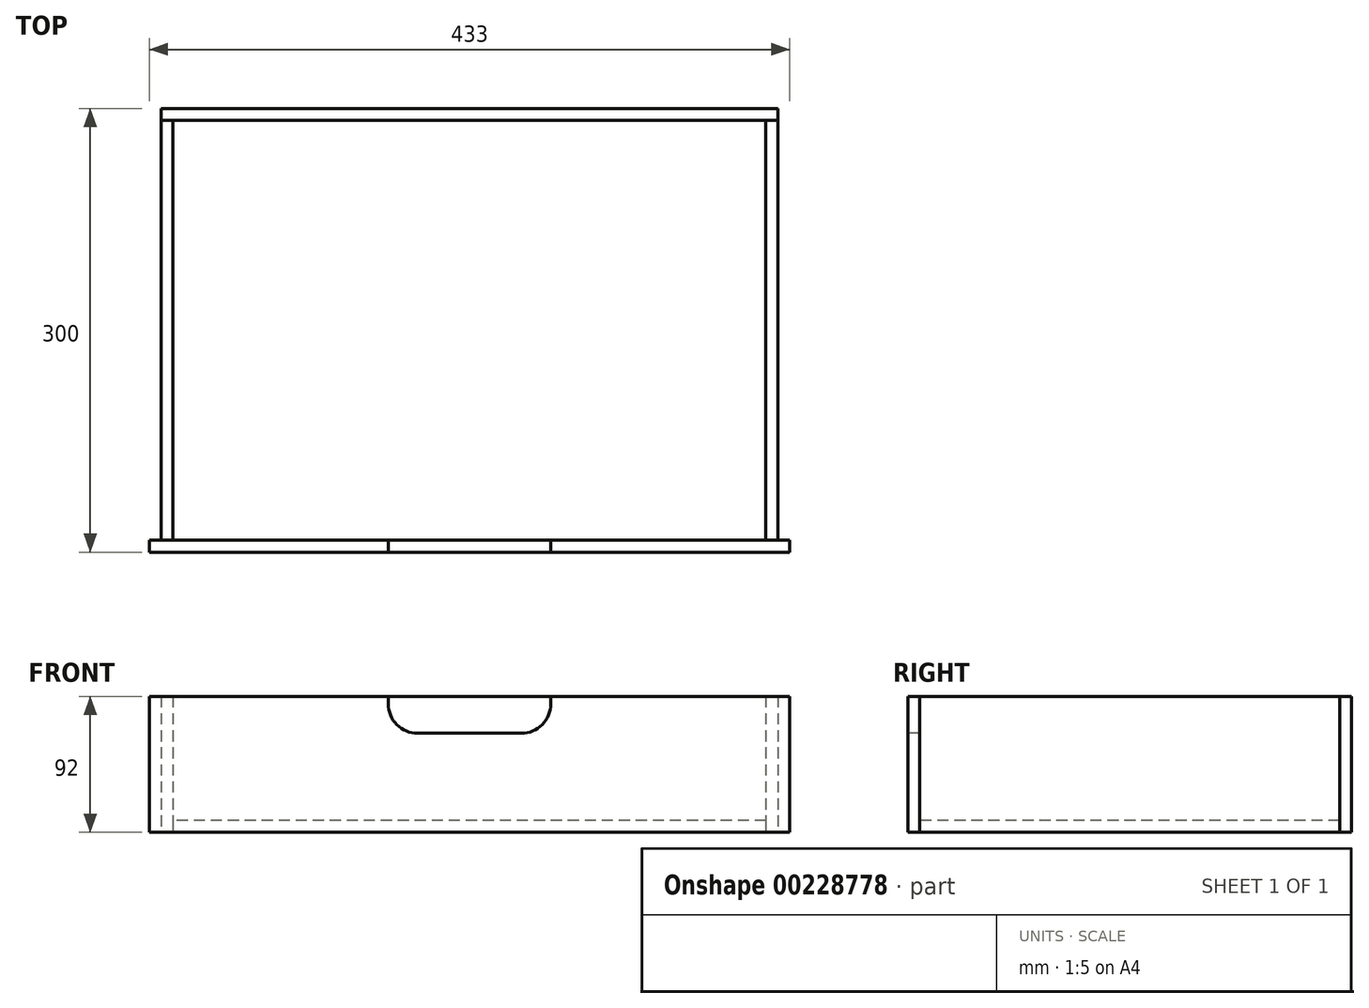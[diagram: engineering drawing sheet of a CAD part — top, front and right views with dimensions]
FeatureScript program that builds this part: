
annotation { "Feature Type Name" : "Feature", "Feature Type Description" : "" }
export const myFeature = defineFeature(function(context is Context, id is Id, definition is map)
    precondition{}
    {
        {
            var Q0;
            Q0=qCreatedBy(makeId("Front.planeOp"),FACE);
            var sketch = newSketch(context, id + "F0", { "sketchPlane" : qUnion([Q0])});
            skLineSegment(sketch, "E0.bottom", {"start": v(216.5, 46) * mm, "end": v(-216.5, 46) * mm});
            skLineSegment(sketch, "E0.top", {"start": v(216.5, -46) * mm, "end": v(-216.5, -46) * mm});
            skLineSegment(sketch, "E0.left", {"start": v(216.5, 46) * mm, "end": v(216.5, -46) * mm});
            skLineSegment(sketch, "E0.right", {"start": v(-216.5, 46) * mm, "end": v(-216.5, -46) * mm});
            skPoint(sketch, "E0.middle", {"position": v(0, 0) * mm});
            skSolve(sketch);
        }
        {
            var Q0;
            Q0=makeQuery(id+"F0.imprint","IMPRINT",FACE,{"disambiguationData":[TD([[makeQuery(id+"F0.imprint","IMPRINT",EDGE,{"derivedFrom":sQuery(id+"F0.wireOp",EDGE,"E0.bottom")}),1.0]])]});
            extrude(context, id + "F1", {"entities" : qUnion([Q0]), "depth" : 8 * mm});
        }
        {
            var Q0;
            Q0=makeQuery(id+"F1.opExtrude","CAP_FACE",FACE,{"disambiguationData":[OSD([sQuery(id+"F0.wireOp",EDGE,"E0.bottom"),sQuery(id+"F0.wireOp",EDGE,"E0.top"),sQuery(id+"F0.wireOp",EDGE,"E0.left"),sQuery(id+"F0.wireOp",EDGE,"E0.right")])],"isStart":false});
            var sketch = newSketch(context, id + "F2", { "sketchPlane" : qUnion([Q0])});
            skLineSegment(sketch, "E1.bottom", {"start": v(55, 21) * mm, "end": v(-55, 21) * mm});
            skLineSegment(sketch, "E1.top", {"start": v(55, 46) * mm, "end": v(-55, 46) * mm});
            skLineSegment(sketch, "E1.left", {"start": v(55, 21) * mm, "end": v(55, 46) * mm});
            skLineSegment(sketch, "E1.right", {"start": v(-55, 21) * mm, "end": v(-55, 46) * mm});
            skPoint(sketch, "E1.middle", {"position": v(0, 33.5) * mm});
            skSolve(sketch);
        }
        {
            var Q0;
            Q0=makeQuery(id+"F2.imprint","IMPRINT",FACE,{"disambiguationData":[TD([[makeQuery(id+"F2.imprint","IMPRINT",EDGE,{"derivedFrom":sQuery(id+"F2.wireOp",EDGE,"E1.bottom")}),-1.0]])]});
            extrude(context, id + "F3", {"entities" : qUnion([Q0]), "operationType" : NewBodyOperationType.REMOVE, "endBound" : BoundingType.UP_TO_NEXT, "oppositeDirection" : true, "depth" : 25 * mm});
        }
        {
            var Q0;
            Q0=makeQuery(id+"F3.boolean.opBoolean","COPY",EDGE,{"derivedFrom":makeQuery(id+"F3.opExtrude","SWEPT_EDGE",EDGE,{"disambiguationData":[OSD([sQuery(id+"F2.wireOp",EDGE,"E1.bottom"),sQuery(id+"F2.wireOp",EDGE,"E1.right")])]})});
            var Q1;
            Q1=makeQuery(id+"F3.boolean.opBoolean","COPY",EDGE,{"derivedFrom":makeQuery(id+"F3.opExtrude","SWEPT_EDGE",EDGE,{"disambiguationData":[OSD([sQuery(id+"F2.wireOp",EDGE,"E1.bottom"),sQuery(id+"F2.wireOp",EDGE,"E1.left")])]})});
            fillet(context, id + "F4", {"entities" : qUnion([Q0, Q1]), "radius" : 20 * mm, "tangentPropagation" : true, "allowEdgeOverflow" : false});
        }
        {
            var Q0;
            Q0=makeQuery(id+"F1.opExtrude","CAP_FACE",FACE,{"disambiguationData":[OSD([sQuery(id+"F0.wireOp",EDGE,"E0.bottom"),sQuery(id+"F0.wireOp",EDGE,"E0.top"),sQuery(id+"F0.wireOp",EDGE,"E0.left"),sQuery(id+"F0.wireOp",EDGE,"E0.right")])],"isStart":true});
            var sketch = newSketch(context, id + "F5", { "sketchPlane" : qUnion([Q0])});
            skLineSegment(sketch, "E2.bottom", {"start": v(208.5, 46) * mm, "end": v(200.5, 46) * mm});
            skLineSegment(sketch, "E2.top", {"start": v(208.5, -46) * mm, "end": v(200.5, -46) * mm});
            skLineSegment(sketch, "E2.left", {"start": v(208.5, 46) * mm, "end": v(208.5, -46) * mm});
            skLineSegment(sketch, "E2.right", {"start": v(200.5, 46) * mm, "end": v(200.5, -46) * mm});
            skSolve(sketch);
        }
        {
            var Q0;
            Q0=makeQuery(id+"F5.imprint","IMPRINT",FACE,{"disambiguationData":[TD([[makeQuery(id+"F5.imprint","IMPRINT",EDGE,{"derivedFrom":sQuery(id+"F5.wireOp",EDGE,"E2.bottom")}),-1.0]])]});
            extrude(context, id + "F6", {"entities" : qUnion([Q0]), "depth" : (300 - 16) * mm});
        }
        {
            var Q0;
            Q0=makeQuery(id+"F6.opExtrude","SWEPT_BODY",BODY,{"disambiguationData":[OSD([sQuery(id+"F5.wireOp",EDGE,"E2.bottom"),sQuery(id+"F5.wireOp",EDGE,"E2.top"),sQuery(id+"F5.wireOp",EDGE,"E2.left"),sQuery(id+"F5.wireOp",EDGE,"E2.right")])]});
            var Q1;
            Q1=qCreatedBy(makeId("Right.planeOp"),FACE);
            mirror(context, id + "F7", {"entities" : qUnion([Q0]), "mirrorPlane" : qUnion([Q1])});
        }
        {
            var Q0;
            Q0=makeQuery(id+"F7.opPattern","COPY",FACE,{"derivedFrom":makeQuery(id+"F6.opExtrude","CAP_FACE",FACE,{"disambiguationData":[OSD([sQuery(id+"F5.wireOp",EDGE,"E2.bottom"),sQuery(id+"F5.wireOp",EDGE,"E2.top"),sQuery(id+"F5.wireOp",EDGE,"E2.left"),sQuery(id+"F5.wireOp",EDGE,"E2.right")])],"isStart":false}),"instanceName":"1"});
            var sketch = newSketch(context, id + "F8", { "sketchPlane" : qUnion([Q0])});
            skLineSegment(sketch, "E3.bottom", {"start": v(-208.5, 46) * mm, "end": v(208.5, 46) * mm});
            skLineSegment(sketch, "E3.top", {"start": v(-208.5, -46) * mm, "end": v(208.5, -46) * mm});
            skLineSegment(sketch, "E3.left", {"start": v(-208.5, 46) * mm, "end": v(-208.5, -46) * mm});
            skLineSegment(sketch, "E3.right", {"start": v(208.5, 46) * mm, "end": v(208.5, -46) * mm});
            skSolve(sketch);
        }
        {
            var Q0;
            Q0 = qSketchRegion(id + "F8", true);
            extrude(context, id + "F9", {"entities" : qUnion([Q0]), "depth" : 8 * mm});
        }
        {
            var Q0;
            Q0=makeQuery(id+"F7.opPattern","COPY",FACE,{"derivedFrom":makeQuery(id+"F6.opExtrude","SWEPT_FACE",FACE,{"disambiguationData":[OSD([sQuery(id+"F5.wireOp",EDGE,"E2.top")])]}),"instanceName":"1"});
            var sketch = newSketch(context, id + "F10", { "sketchPlane" : qUnion([Q0])});
            skLineSegment(sketch, "E4.bottom", {"start": v(200.5, -284) * mm, "end": v(-200.5, -284) * mm});
            skLineSegment(sketch, "E4.top", {"start": v(200.5, 0) * mm, "end": v(-200.5, 0) * mm});
            skLineSegment(sketch, "E4.left", {"start": v(200.5, -284) * mm, "end": v(200.5, 0) * mm});
            skLineSegment(sketch, "E4.right", {"start": v(-200.5, -284) * mm, "end": v(-200.5, 0) * mm});
            skSolve(sketch);
        }
        {
            var Q0;
            Q0=makeQuery(id+"F10.imprint","IMPRINT",FACE,{"disambiguationData":[TD([[makeQuery(id+"F10.imprint","IMPRINT",EDGE,{"derivedFrom":sQuery(id+"F10.wireOp",EDGE,"E4.bottom")}),-1.0]])]});
            extrude(context, id + "F11", {"entities" : qUnion([Q0]), "oppositeDirection" : true, "depth" : 8 * mm});
        }
    });
